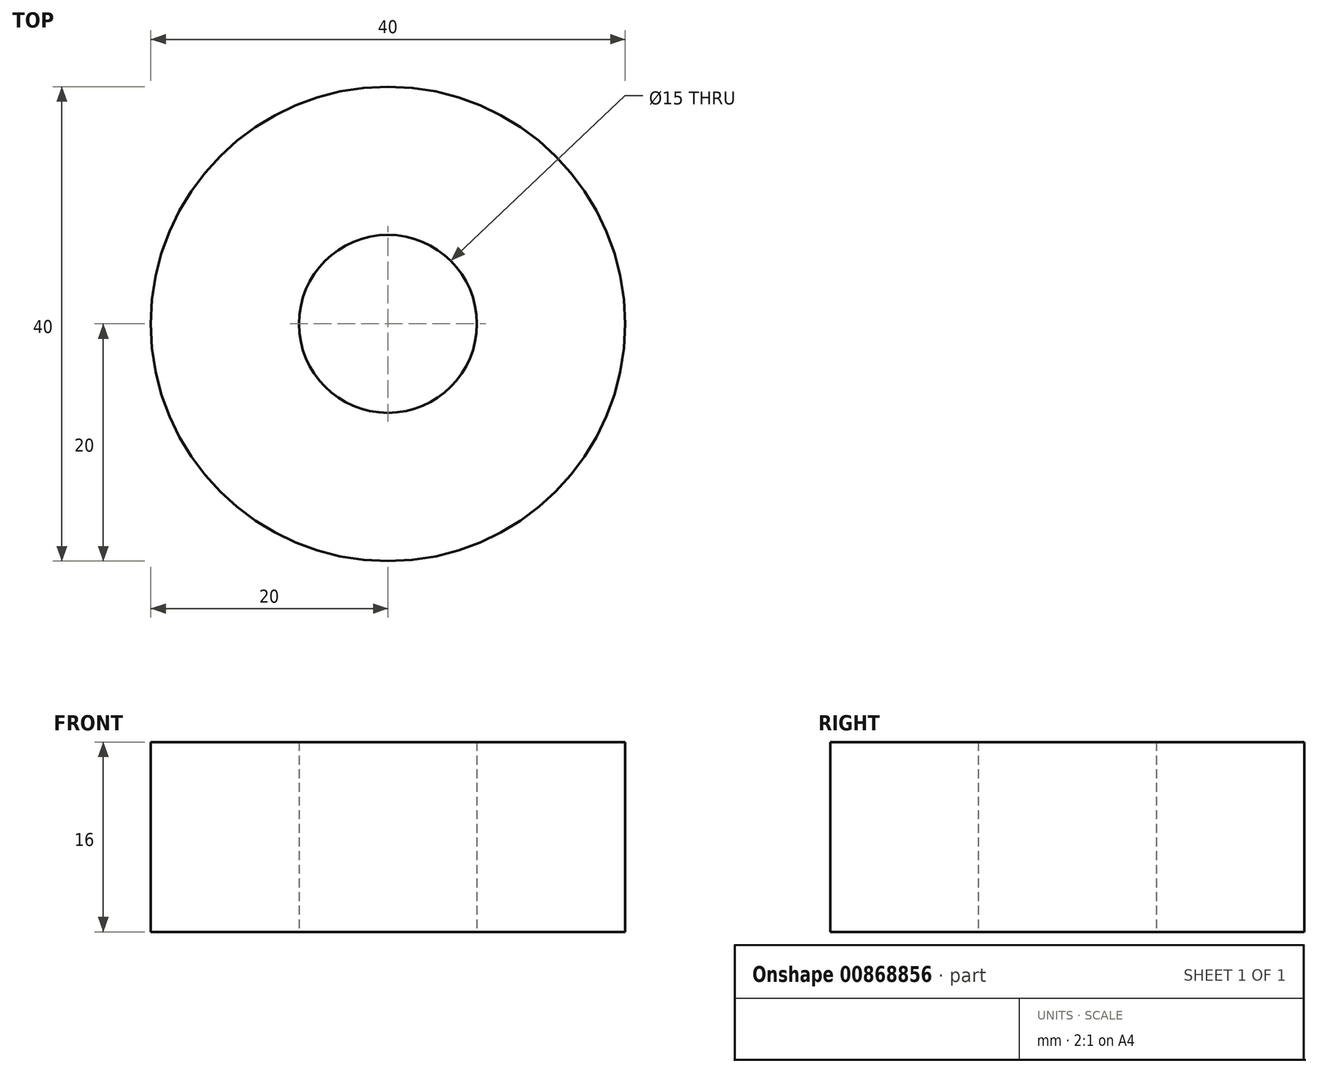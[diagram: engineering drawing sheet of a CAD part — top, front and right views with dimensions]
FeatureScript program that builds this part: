
annotation { "Feature Type Name" : "Feature", "Feature Type Description" : "" }
export const myFeature = defineFeature(function(context is Context, id is Id, definition is map)
    precondition{}
    {
        {
            var Q0;
            Q0=qCreatedBy(makeId("Top.planeOp"),FACE);
            var sketch = newSketch(context, id + "F0", { "sketchPlane" : qUnion([Q0])});
            skCircle(sketch, "E0", {"center": v(0, 0) * mm, "radius": 7.5 * mm});
            skCircle(sketch, "E1", {"center": v(0, 0) * mm, "radius": 20 * mm});
            skSolve(sketch);
        }
        {
            var Q0;
            Q0=makeQuery(id+"F0.imprint","IMPRINT",FACE,{"disambiguationData":[TD([[makeQuery(id+"F0.imprint","IMPRINT",EDGE,{"derivedFrom":sQuery(id+"F0.wireOp",EDGE,"E0")}),-1.0]])]});
            extrude(context, id + "F1", {"entities" : qUnion([Q0]), "depth" : 16 * mm, "offsetDistance" : 25 * mm});
        }
    });
